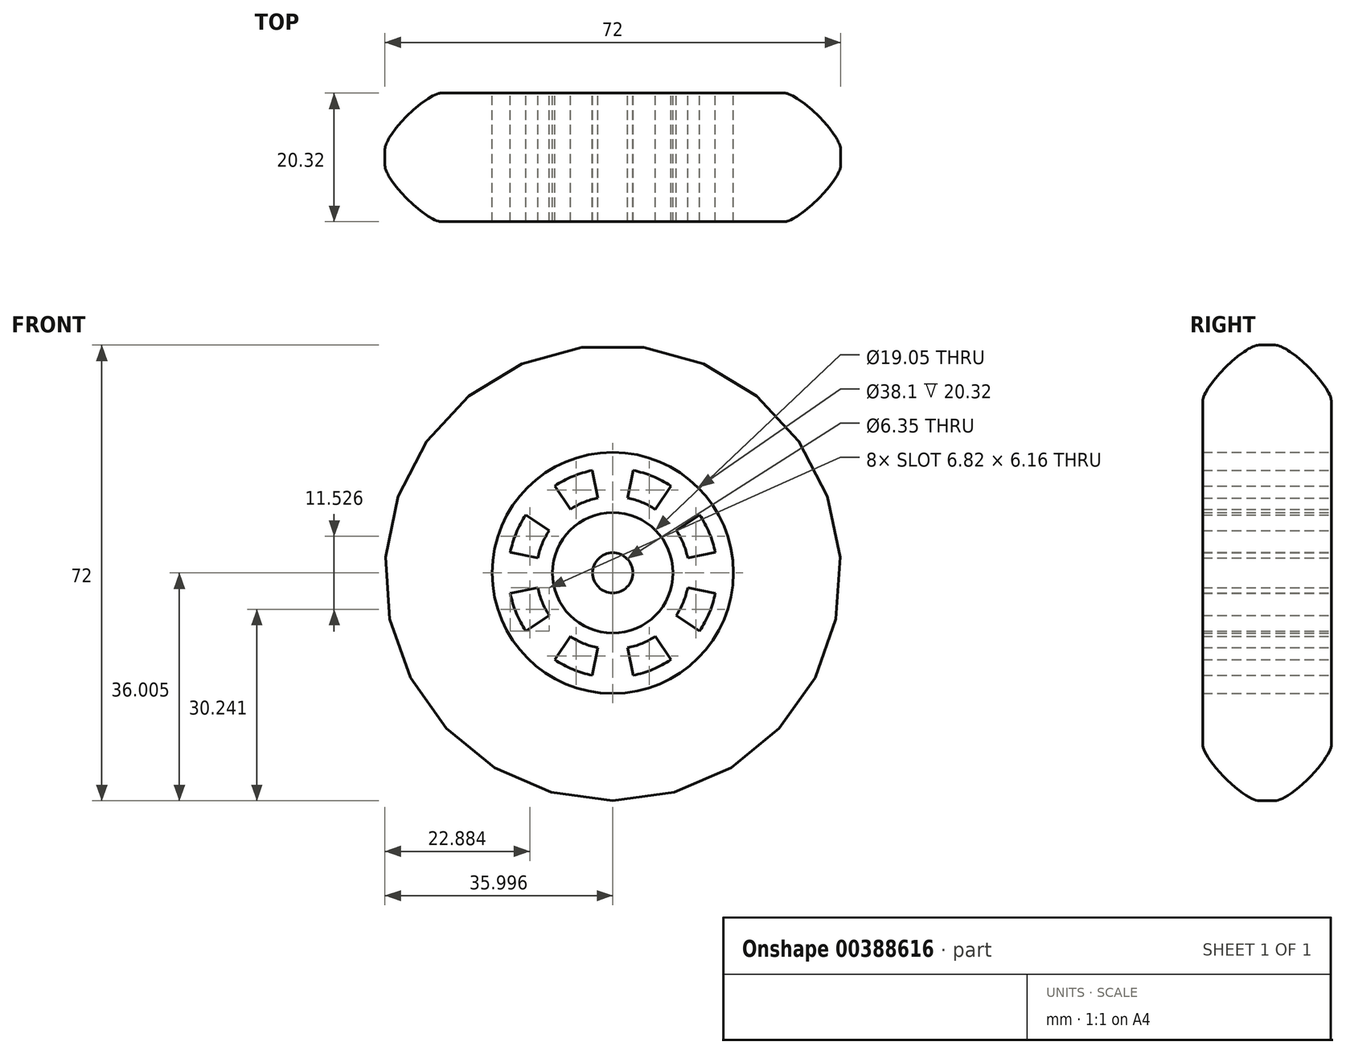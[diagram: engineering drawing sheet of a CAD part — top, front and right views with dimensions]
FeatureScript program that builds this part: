
annotation { "Feature Type Name" : "Feature", "Feature Type Description" : "" }
export const myFeature = defineFeature(function(context is Context, id is Id, definition is map)
    precondition{}
    {
        {
            var Q0;
            Q0=qCreatedBy(makeId("Front.planeOp"),FACE);
            var sketch = newSketch(context, id + "F0", { "sketchPlane" : qUnion([Q0])});
            skCircle(sketch, "E0", {"center": v(-20.8, 25.46) * mm, "radius": 36 * mm});
            skCircle(sketch, "E1", {"center": v(-20.8, 25.46) * mm, "radius": 19.05 * mm});
            skCircle(sketch, "E2", {"center": v(-20.8, 25.46) * mm, "radius": 9.53 * mm});
            skCircle(sketch, "E3", {"center": v(-20.8, 25.46) * mm, "radius": 3.18 * mm});
            skCircle(sketch, "E4", {"center": v(-20.8, 25.46) * mm, "radius": 16.51 * mm});
            skCircle(sketch, "E5", {"center": v(-20.8, 25.46) * mm, "radius": 12.07 * mm});
            skPoint(sketch, "E6.0.midPoint", {"position": v(-20.8, 41.97) * mm});
            skLineSegment(sketch, "E7", {"start": v(-30.15, 39.46) * mm, "end": v(-20.8, 25.46) * mm});
            skLineSegment(sketch, "E8", {"start": v(-24.08, 41.97) * mm, "end": v(-20.8, 25.46) * mm});
            skLineSegment(sketch, "E9", {"start": v(-17.5, 41.97) * mm, "end": v(-20.8, 25.46) * mm});
            skLineSegment(sketch, "E10", {"start": v(-11.44, 39.46) * mm, "end": v(-20.8, 25.46) * mm});
            skLineSegment(sketch, "E11", {"start": v(-6.8, 34.82) * mm, "end": v(-20.8, 25.46) * mm});
            skLineSegment(sketch, "E12", {"start": v(-4.28, 28.75) * mm, "end": v(-20.8, 25.46) * mm});
            skLineSegment(sketch, "E13", {"start": v(-4.28, 22.18) * mm, "end": v(-20.8, 25.46) * mm});
            skLineSegment(sketch, "E14", {"start": v(-6.8, 16.11) * mm, "end": v(-20.8, 25.46) * mm});
            skLineSegment(sketch, "E15", {"start": v(-11.44, 11.47) * mm, "end": v(-20.8, 25.46) * mm});
            skLineSegment(sketch, "E16", {"start": v(-17.5, 8.95) * mm, "end": v(-20.8, 25.46) * mm});
            skLineSegment(sketch, "E17", {"start": v(-24.08, 8.95) * mm, "end": v(-20.8, 25.46) * mm});
            skLineSegment(sketch, "E18", {"start": v(-30.15, 11.47) * mm, "end": v(-20.8, 25.46) * mm});
            skLineSegment(sketch, "E19", {"start": v(-34.8, 16.11) * mm, "end": v(-20.8, 25.46) * mm});
            skLineSegment(sketch, "E20", {"start": v(-37.3, 22.18) * mm, "end": v(-20.8, 25.46) * mm});
            skLineSegment(sketch, "E21", {"start": v(-37.3, 28.75) * mm, "end": v(-20.8, 25.46) * mm});
            skLineSegment(sketch, "E22", {"start": v(-34.8, 34.82) * mm, "end": v(-20.8, 25.46) * mm});
            skSolve(sketch);
        }
        {
            var Q0;
            {var subQ0=sQuery(id+"F0.wireOp",EDGE,"E8");var subQ1=sQuery(id+"F0.wireOp",EDGE,"E2");var subQ2=makeQuery(id+"F0.imprint","INTERSECT",VERTEX,{"derivedFrom":[subQ1,subQ0]});Q0=makeQuery(id+"F0.imprint","IMPRINT",FACE,{"disambiguationData":[TD([[makeQuery(id+"F0.imprint","IMPRINT",EDGE,{"disambiguationData":[TD([[subQ2,-1.0]])],"derivedFrom":subQ1}),1.0]])]});}
            var Q1;
            {var subQ0=sQuery(id+"F0.wireOp",EDGE,"E9");var subQ1=sQuery(id+"F0.wireOp",EDGE,"E2");var subQ2=makeQuery(id+"F0.imprint","INTERSECT",VERTEX,{"derivedFrom":[subQ1,subQ0]});Q1=makeQuery(id+"F0.imprint","IMPRINT",FACE,{"disambiguationData":[TD([[makeQuery(id+"F0.imprint","IMPRINT",EDGE,{"disambiguationData":[TD([[subQ2,-1.0]])],"derivedFrom":subQ1}),1.0]])]});}
            var Q2;
            {var subQ0=sQuery(id+"F0.wireOp",EDGE,"E10");var subQ1=sQuery(id+"F0.wireOp",EDGE,"E2");var subQ2=makeQuery(id+"F0.imprint","INTERSECT",VERTEX,{"derivedFrom":[subQ1,subQ0]});Q2=makeQuery(id+"F0.imprint","IMPRINT",FACE,{"disambiguationData":[TD([[makeQuery(id+"F0.imprint","IMPRINT",EDGE,{"disambiguationData":[TD([[subQ2,-1.0]])],"derivedFrom":subQ1}),1.0]])]});}
            var Q3;
            {var subQ0=sQuery(id+"F0.wireOp",EDGE,"E11");var subQ1=sQuery(id+"F0.wireOp",EDGE,"E2");var subQ2=makeQuery(id+"F0.imprint","INTERSECT",VERTEX,{"derivedFrom":[subQ1,subQ0]});Q3=makeQuery(id+"F0.imprint","IMPRINT",FACE,{"disambiguationData":[TD([[makeQuery(id+"F0.imprint","IMPRINT",EDGE,{"disambiguationData":[TD([[subQ2,-1.0]])],"derivedFrom":subQ1}),1.0]])]});}
            var Q4;
            {var subQ0=sQuery(id+"F0.wireOp",EDGE,"E11");var subQ1=sQuery(id+"F0.wireOp",EDGE,"E2");var subQ2=makeQuery(id+"F0.imprint","INTERSECT",VERTEX,{"derivedFrom":[subQ1,subQ0]});Q4=makeQuery(id+"F0.imprint","IMPRINT",FACE,{"disambiguationData":[TD([[makeQuery(id+"F0.imprint","IMPRINT",EDGE,{"disambiguationData":[TD([[subQ2,1.0]])],"derivedFrom":subQ1}),1.0]])]});}
            var Q5;
            {var subQ0=sQuery(id+"F0.wireOp",EDGE,"E7");var subQ1=sQuery(id+"F0.wireOp",EDGE,"E2");var subQ2=makeQuery(id+"F0.imprint","INTERSECT",VERTEX,{"derivedFrom":[subQ1,subQ0]});Q5=makeQuery(id+"F0.imprint","IMPRINT",FACE,{"disambiguationData":[TD([[makeQuery(id+"F0.imprint","IMPRINT",EDGE,{"disambiguationData":[TD([[subQ2,-1.0]])],"derivedFrom":subQ1}),1.0]])]});}
            var Q6;
            {var subQ0=sQuery(id+"F0.wireOp",EDGE,"E22");var subQ1=sQuery(id+"F0.wireOp",EDGE,"E2");var subQ2=makeQuery(id+"F0.imprint","INTERSECT",VERTEX,{"derivedFrom":[subQ1,subQ0]});Q6=makeQuery(id+"F0.imprint","IMPRINT",FACE,{"disambiguationData":[TD([[makeQuery(id+"F0.imprint","IMPRINT",EDGE,{"disambiguationData":[TD([[subQ2,-1.0]])],"derivedFrom":subQ1}),1.0]])]});}
            var Q7;
            {var subQ0=sQuery(id+"F0.wireOp",EDGE,"E21");var subQ1=sQuery(id+"F0.wireOp",EDGE,"E2");var subQ2=makeQuery(id+"F0.imprint","INTERSECT",VERTEX,{"derivedFrom":[subQ1,subQ0]});Q7=makeQuery(id+"F0.imprint","IMPRINT",FACE,{"disambiguationData":[TD([[makeQuery(id+"F0.imprint","IMPRINT",EDGE,{"disambiguationData":[TD([[subQ2,-1.0]])],"derivedFrom":subQ1}),1.0]])]});}
            var Q8;
            {var subQ0=sQuery(id+"F0.wireOp",EDGE,"E20");var subQ1=sQuery(id+"F0.wireOp",EDGE,"E2");var subQ2=makeQuery(id+"F0.imprint","INTERSECT",VERTEX,{"derivedFrom":[subQ1,subQ0]});Q8=makeQuery(id+"F0.imprint","IMPRINT",FACE,{"disambiguationData":[TD([[makeQuery(id+"F0.imprint","IMPRINT",EDGE,{"disambiguationData":[TD([[subQ2,-1.0]])],"derivedFrom":subQ1}),1.0]])]});}
            var Q9;
            {var subQ0=sQuery(id+"F0.wireOp",EDGE,"E19");var subQ1=sQuery(id+"F0.wireOp",EDGE,"E2");var subQ2=makeQuery(id+"F0.imprint","INTERSECT",VERTEX,{"derivedFrom":[subQ1,subQ0]});Q9=makeQuery(id+"F0.imprint","IMPRINT",FACE,{"disambiguationData":[TD([[makeQuery(id+"F0.imprint","IMPRINT",EDGE,{"disambiguationData":[TD([[subQ2,-1.0]])],"derivedFrom":subQ1}),1.0]])]});}
            var Q10;
            {var subQ0=sQuery(id+"F0.wireOp",EDGE,"E18");var subQ1=sQuery(id+"F0.wireOp",EDGE,"E2");var subQ2=makeQuery(id+"F0.imprint","INTERSECT",VERTEX,{"derivedFrom":[subQ1,subQ0]});Q10=makeQuery(id+"F0.imprint","IMPRINT",FACE,{"disambiguationData":[TD([[makeQuery(id+"F0.imprint","IMPRINT",EDGE,{"disambiguationData":[TD([[subQ2,-1.0]])],"derivedFrom":subQ1}),1.0]])]});}
            var Q11;
            {var subQ0=sQuery(id+"F0.wireOp",EDGE,"E17");var subQ1=sQuery(id+"F0.wireOp",EDGE,"E2");var subQ2=makeQuery(id+"F0.imprint","INTERSECT",VERTEX,{"derivedFrom":[subQ1,subQ0]});Q11=makeQuery(id+"F0.imprint","IMPRINT",FACE,{"disambiguationData":[TD([[makeQuery(id+"F0.imprint","IMPRINT",EDGE,{"disambiguationData":[TD([[subQ2,-1.0]])],"derivedFrom":subQ1}),1.0]])]});}
            var Q12;
            {var subQ0=sQuery(id+"F0.wireOp",EDGE,"E16");var subQ1=sQuery(id+"F0.wireOp",EDGE,"E2");var subQ2=makeQuery(id+"F0.imprint","INTERSECT",VERTEX,{"derivedFrom":[subQ1,subQ0]});Q12=makeQuery(id+"F0.imprint","IMPRINT",FACE,{"disambiguationData":[TD([[makeQuery(id+"F0.imprint","IMPRINT",EDGE,{"disambiguationData":[TD([[subQ2,-1.0]])],"derivedFrom":subQ1}),1.0]])]});}
            var Q13;
            {var subQ0=sQuery(id+"F0.wireOp",EDGE,"E15");var subQ1=sQuery(id+"F0.wireOp",EDGE,"E2");var subQ2=makeQuery(id+"F0.imprint","INTERSECT",VERTEX,{"derivedFrom":[subQ1,subQ0]});Q13=makeQuery(id+"F0.imprint","IMPRINT",FACE,{"disambiguationData":[TD([[makeQuery(id+"F0.imprint","IMPRINT",EDGE,{"disambiguationData":[TD([[subQ2,-1.0]])],"derivedFrom":subQ1}),1.0]])]});}
            var Q14;
            {var subQ0=sQuery(id+"F0.wireOp",EDGE,"E14");var subQ1=sQuery(id+"F0.wireOp",EDGE,"E2");var subQ2=makeQuery(id+"F0.imprint","INTERSECT",VERTEX,{"derivedFrom":[subQ1,subQ0]});Q14=makeQuery(id+"F0.imprint","IMPRINT",FACE,{"disambiguationData":[TD([[makeQuery(id+"F0.imprint","IMPRINT",EDGE,{"disambiguationData":[TD([[subQ2,-1.0]])],"derivedFrom":subQ1}),1.0]])]});}
            var Q15;
            {var subQ0=sQuery(id+"F0.wireOp",EDGE,"E12");var subQ1=sQuery(id+"F0.wireOp",EDGE,"E2");var subQ2=makeQuery(id+"F0.imprint","INTERSECT",VERTEX,{"derivedFrom":[subQ1,subQ0]});Q15=makeQuery(id+"F0.imprint","IMPRINT",FACE,{"disambiguationData":[TD([[makeQuery(id+"F0.imprint","IMPRINT",EDGE,{"disambiguationData":[TD([[subQ2,1.0]])],"derivedFrom":subQ1}),1.0]])]});}
            extrude(context, id + "F1", {"entities" : qUnion([Q0, Q1, Q2, Q3, Q4, Q5, Q6, Q7, Q8, Q9, Q10, Q11, Q12, Q13, Q14, Q15]), "depth" : 20.32 * mm});
        }
        {
            var Q0;
            {var subQ0=sQuery(id+"F0.wireOp",EDGE,"E8");var subQ1=sQuery(id+"F0.wireOp",EDGE,"E2");var subQ2=makeQuery(id+"F0.imprint","INTERSECT",VERTEX,{"derivedFrom":[subQ1,subQ0]});Q0=makeQuery(id+"F0.imprint","IMPRINT",FACE,{"disambiguationData":[TD([[makeQuery(id+"F0.imprint","IMPRINT",EDGE,{"disambiguationData":[TD([[subQ2,-1.0]])],"derivedFrom":subQ1}),-1.0]])]});}
            var Q1;
            {var subQ0=sQuery(id+"F0.wireOp",EDGE,"E7");var subQ1=sQuery(id+"F0.wireOp",EDGE,"E2");var subQ2=makeQuery(id+"F0.imprint","INTERSECT",VERTEX,{"derivedFrom":[subQ1,subQ0]});Q1=makeQuery(id+"F0.imprint","IMPRINT",FACE,{"disambiguationData":[TD([[makeQuery(id+"F0.imprint","IMPRINT",EDGE,{"disambiguationData":[TD([[subQ2,-1.0]])],"derivedFrom":subQ1}),-1.0]])]});}
            var Q2;
            {var subQ0=sQuery(id+"F0.wireOp",EDGE,"E7");var subQ1=sQuery(id+"F0.wireOp",EDGE,"E4");var subQ2=makeQuery(id+"F0.imprint","INTERSECT",VERTEX,{"derivedFrom":[subQ1,subQ0]});Q2=makeQuery(id+"F0.imprint","IMPRINT",FACE,{"disambiguationData":[TD([[makeQuery(id+"F0.imprint","IMPRINT",EDGE,{"disambiguationData":[TD([[subQ2,-1.0]])],"derivedFrom":subQ1}),1.0]])]});}
            var Q3;
            {var subQ0=sQuery(id+"F0.wireOp",EDGE,"E22");var subQ1=sQuery(id+"F0.wireOp",EDGE,"E2");var subQ2=makeQuery(id+"F0.imprint","INTERSECT",VERTEX,{"derivedFrom":[subQ1,subQ0]});Q3=makeQuery(id+"F0.imprint","IMPRINT",FACE,{"disambiguationData":[TD([[makeQuery(id+"F0.imprint","IMPRINT",EDGE,{"disambiguationData":[TD([[subQ2,-1.0]])],"derivedFrom":subQ1}),-1.0]])]});}
            var Q4;
            {var subQ0=sQuery(id+"F0.wireOp",EDGE,"E21");var subQ1=sQuery(id+"F0.wireOp",EDGE,"E4");var subQ2=makeQuery(id+"F0.imprint","INTERSECT",VERTEX,{"derivedFrom":[subQ1,subQ0]});Q4=makeQuery(id+"F0.imprint","IMPRINT",FACE,{"disambiguationData":[TD([[makeQuery(id+"F0.imprint","IMPRINT",EDGE,{"disambiguationData":[TD([[subQ2,-1.0]])],"derivedFrom":subQ1}),1.0]])]});}
            var Q5;
            {var subQ0=sQuery(id+"F0.wireOp",EDGE,"E21");var subQ1=sQuery(id+"F0.wireOp",EDGE,"E2");var subQ2=makeQuery(id+"F0.imprint","INTERSECT",VERTEX,{"derivedFrom":[subQ1,subQ0]});Q5=makeQuery(id+"F0.imprint","IMPRINT",FACE,{"disambiguationData":[TD([[makeQuery(id+"F0.imprint","IMPRINT",EDGE,{"disambiguationData":[TD([[subQ2,-1.0]])],"derivedFrom":subQ1}),-1.0]])]});}
            var Q6;
            {var subQ0=sQuery(id+"F0.wireOp",EDGE,"E20");var subQ1=sQuery(id+"F0.wireOp",EDGE,"E2");var subQ2=makeQuery(id+"F0.imprint","INTERSECT",VERTEX,{"derivedFrom":[subQ1,subQ0]});Q6=makeQuery(id+"F0.imprint","IMPRINT",FACE,{"disambiguationData":[TD([[makeQuery(id+"F0.imprint","IMPRINT",EDGE,{"disambiguationData":[TD([[subQ2,-1.0]])],"derivedFrom":subQ1}),-1.0]])]});}
            var Q7;
            {var subQ0=sQuery(id+"F0.wireOp",EDGE,"E19");var subQ1=sQuery(id+"F0.wireOp",EDGE,"E2");var subQ2=makeQuery(id+"F0.imprint","INTERSECT",VERTEX,{"derivedFrom":[subQ1,subQ0]});Q7=makeQuery(id+"F0.imprint","IMPRINT",FACE,{"disambiguationData":[TD([[makeQuery(id+"F0.imprint","IMPRINT",EDGE,{"disambiguationData":[TD([[subQ2,-1.0]])],"derivedFrom":subQ1}),-1.0]])]});}
            var Q8;
            {var subQ0=sQuery(id+"F0.wireOp",EDGE,"E19");var subQ1=sQuery(id+"F0.wireOp",EDGE,"E4");var subQ2=makeQuery(id+"F0.imprint","INTERSECT",VERTEX,{"derivedFrom":[subQ1,subQ0]});Q8=makeQuery(id+"F0.imprint","IMPRINT",FACE,{"disambiguationData":[TD([[makeQuery(id+"F0.imprint","IMPRINT",EDGE,{"disambiguationData":[TD([[subQ2,-1.0]])],"derivedFrom":subQ1}),1.0]])]});}
            var Q9;
            {var subQ0=sQuery(id+"F0.wireOp",EDGE,"E18");var subQ1=sQuery(id+"F0.wireOp",EDGE,"E2");var subQ2=makeQuery(id+"F0.imprint","INTERSECT",VERTEX,{"derivedFrom":[subQ1,subQ0]});Q9=makeQuery(id+"F0.imprint","IMPRINT",FACE,{"disambiguationData":[TD([[makeQuery(id+"F0.imprint","IMPRINT",EDGE,{"disambiguationData":[TD([[subQ2,-1.0]])],"derivedFrom":subQ1}),-1.0]])]});}
            var Q10;
            {var subQ0=sQuery(id+"F0.wireOp",EDGE,"E17");var subQ1=sQuery(id+"F0.wireOp",EDGE,"E2");var subQ2=makeQuery(id+"F0.imprint","INTERSECT",VERTEX,{"derivedFrom":[subQ1,subQ0]});Q10=makeQuery(id+"F0.imprint","IMPRINT",FACE,{"disambiguationData":[TD([[makeQuery(id+"F0.imprint","IMPRINT",EDGE,{"disambiguationData":[TD([[subQ2,-1.0]])],"derivedFrom":subQ1}),-1.0]])]});}
            var Q11;
            {var subQ0=sQuery(id+"F0.wireOp",EDGE,"E17");var subQ1=sQuery(id+"F0.wireOp",EDGE,"E4");var subQ2=makeQuery(id+"F0.imprint","INTERSECT",VERTEX,{"derivedFrom":[subQ1,subQ0]});Q11=makeQuery(id+"F0.imprint","IMPRINT",FACE,{"disambiguationData":[TD([[makeQuery(id+"F0.imprint","IMPRINT",EDGE,{"disambiguationData":[TD([[subQ2,-1.0]])],"derivedFrom":subQ1}),1.0]])]});}
            var Q12;
            {var subQ0=sQuery(id+"F0.wireOp",EDGE,"E16");var subQ1=sQuery(id+"F0.wireOp",EDGE,"E2");var subQ2=makeQuery(id+"F0.imprint","INTERSECT",VERTEX,{"derivedFrom":[subQ1,subQ0]});Q12=makeQuery(id+"F0.imprint","IMPRINT",FACE,{"disambiguationData":[TD([[makeQuery(id+"F0.imprint","IMPRINT",EDGE,{"disambiguationData":[TD([[subQ2,-1.0]])],"derivedFrom":subQ1}),-1.0]])]});}
            var Q13;
            {var subQ0=sQuery(id+"F0.wireOp",EDGE,"E15");var subQ1=sQuery(id+"F0.wireOp",EDGE,"E2");var subQ2=makeQuery(id+"F0.imprint","INTERSECT",VERTEX,{"derivedFrom":[subQ1,subQ0]});Q13=makeQuery(id+"F0.imprint","IMPRINT",FACE,{"disambiguationData":[TD([[makeQuery(id+"F0.imprint","IMPRINT",EDGE,{"disambiguationData":[TD([[subQ2,-1.0]])],"derivedFrom":subQ1}),-1.0]])]});}
            var Q14;
            {var subQ0=sQuery(id+"F0.wireOp",EDGE,"E14");var subQ1=sQuery(id+"F0.wireOp",EDGE,"E2");var subQ2=makeQuery(id+"F0.imprint","INTERSECT",VERTEX,{"derivedFrom":[subQ1,subQ0]});Q14=makeQuery(id+"F0.imprint","IMPRINT",FACE,{"disambiguationData":[TD([[makeQuery(id+"F0.imprint","IMPRINT",EDGE,{"disambiguationData":[TD([[subQ2,-1.0]])],"derivedFrom":subQ1}),-1.0]])]});}
            var Q15;
            {var subQ0=sQuery(id+"F0.wireOp",EDGE,"E12");var subQ1=sQuery(id+"F0.wireOp",EDGE,"E2");var subQ2=makeQuery(id+"F0.imprint","INTERSECT",VERTEX,{"derivedFrom":[subQ1,subQ0]});Q15=makeQuery(id+"F0.imprint","IMPRINT",FACE,{"disambiguationData":[TD([[makeQuery(id+"F0.imprint","IMPRINT",EDGE,{"disambiguationData":[TD([[subQ2,1.0]])],"derivedFrom":subQ1}),-1.0]])]});}
            var Q16;
            {var subQ0=sQuery(id+"F0.wireOp",EDGE,"E11");var subQ1=sQuery(id+"F0.wireOp",EDGE,"E2");var subQ2=makeQuery(id+"F0.imprint","INTERSECT",VERTEX,{"derivedFrom":[subQ1,subQ0]});Q16=makeQuery(id+"F0.imprint","IMPRINT",FACE,{"disambiguationData":[TD([[makeQuery(id+"F0.imprint","IMPRINT",EDGE,{"disambiguationData":[TD([[subQ2,1.0]])],"derivedFrom":subQ1}),-1.0]])]});}
            var Q17;
            {var subQ0=sQuery(id+"F0.wireOp",EDGE,"E11");var subQ1=sQuery(id+"F0.wireOp",EDGE,"E2");var subQ2=makeQuery(id+"F0.imprint","INTERSECT",VERTEX,{"derivedFrom":[subQ1,subQ0]});Q17=makeQuery(id+"F0.imprint","IMPRINT",FACE,{"disambiguationData":[TD([[makeQuery(id+"F0.imprint","IMPRINT",EDGE,{"disambiguationData":[TD([[subQ2,-1.0]])],"derivedFrom":subQ1}),-1.0]])]});}
            var Q18;
            {var subQ0=sQuery(id+"F0.wireOp",EDGE,"E10");var subQ1=sQuery(id+"F0.wireOp",EDGE,"E2");var subQ2=makeQuery(id+"F0.imprint","INTERSECT",VERTEX,{"derivedFrom":[subQ1,subQ0]});Q18=makeQuery(id+"F0.imprint","IMPRINT",FACE,{"disambiguationData":[TD([[makeQuery(id+"F0.imprint","IMPRINT",EDGE,{"disambiguationData":[TD([[subQ2,-1.0]])],"derivedFrom":subQ1}),-1.0]])]});}
            var Q19;
            {var subQ0=sQuery(id+"F0.wireOp",EDGE,"E9");var subQ1=sQuery(id+"F0.wireOp",EDGE,"E2");var subQ2=makeQuery(id+"F0.imprint","INTERSECT",VERTEX,{"derivedFrom":[subQ1,subQ0]});Q19=makeQuery(id+"F0.imprint","IMPRINT",FACE,{"disambiguationData":[TD([[makeQuery(id+"F0.imprint","IMPRINT",EDGE,{"disambiguationData":[TD([[subQ2,-1.0]])],"derivedFrom":subQ1}),-1.0]])]});}
            var Q20;
            {var subQ0=sQuery(id+"F0.wireOp",EDGE,"E9");var subQ1=sQuery(id+"F0.wireOp",EDGE,"E4");var subQ2=makeQuery(id+"F0.imprint","INTERSECT",VERTEX,{"derivedFrom":[subQ1,subQ0]});Q20=makeQuery(id+"F0.imprint","IMPRINT",FACE,{"disambiguationData":[TD([[makeQuery(id+"F0.imprint","IMPRINT",EDGE,{"disambiguationData":[TD([[subQ2,-1.0]])],"derivedFrom":subQ1}),1.0]])]});}
            var Q21;
            {var subQ0=sQuery(id+"F0.wireOp",EDGE,"E11");var subQ1=sQuery(id+"F0.wireOp",EDGE,"E4");var subQ2=makeQuery(id+"F0.imprint","INTERSECT",VERTEX,{"derivedFrom":[subQ1,subQ0]});Q21=makeQuery(id+"F0.imprint","IMPRINT",FACE,{"disambiguationData":[TD([[makeQuery(id+"F0.imprint","IMPRINT",EDGE,{"disambiguationData":[TD([[subQ2,-1.0]])],"derivedFrom":subQ1}),1.0]])]});}
            var Q22;
            {var subQ0=sQuery(id+"F0.wireOp",EDGE,"E12");var subQ1=sQuery(id+"F0.wireOp",EDGE,"E4");var subQ2=makeQuery(id+"F0.imprint","INTERSECT",VERTEX,{"derivedFrom":[subQ1,subQ0]});Q22=makeQuery(id+"F0.imprint","IMPRINT",FACE,{"disambiguationData":[TD([[makeQuery(id+"F0.imprint","IMPRINT",EDGE,{"disambiguationData":[TD([[subQ2,1.0]])],"derivedFrom":subQ1}),1.0]])]});}
            var Q23;
            {var subQ0=sQuery(id+"F0.wireOp",EDGE,"E15");var subQ1=sQuery(id+"F0.wireOp",EDGE,"E4");var subQ2=makeQuery(id+"F0.imprint","INTERSECT",VERTEX,{"derivedFrom":[subQ1,subQ0]});Q23=makeQuery(id+"F0.imprint","IMPRINT",FACE,{"disambiguationData":[TD([[makeQuery(id+"F0.imprint","IMPRINT",EDGE,{"disambiguationData":[TD([[subQ2,-1.0]])],"derivedFrom":subQ1}),1.0]])]});}
            var Q24;
            Q24=makeQuery(id+"F0.imprint","IMPRINT",FACE,{"disambiguationData":[TD([[makeQuery(id+"F0.imprint","IMPRINT",EDGE,{"derivedFrom":sQuery(id+"F0.wireOp",EDGE,"E1")}),1.0]])]});
            extrude(context, id + "F2", {"entities" : qUnion([Q0, Q1, Q2, Q3, Q4, Q5, Q6, Q7, Q8, Q9, Q10, Q11, Q12, Q13, Q14, Q15, Q16, Q17, Q18, Q19, Q20, Q21, Q22, Q23, Q24]), "depth" : 20.32 * mm});
        }
        {
            var Q0;
            Q0=makeQuery(id+"F0.imprint","IMPRINT",FACE,{"disambiguationData":[TD([[makeQuery(id+"F0.imprint","IMPRINT",EDGE,{"derivedFrom":sQuery(id+"F0.wireOp",EDGE,"E0")}),1.0]])]});
            extrude(context, id + "F3", {"entities" : qUnion([Q0]), "depth" : 20.32 * mm});
        }
        {
            var Q0;
            Q0=makeQuery(id+"F3.opExtrude","CAP_EDGE",EDGE,{"disambiguationData":[OSD([sQuery(id+"F0.wireOp",EDGE,"E0")])],"isStart":false});
            var Q1;
            Q1=makeQuery(id+"F3.opExtrude","CAP_EDGE",EDGE,{"disambiguationData":[OSD([sQuery(id+"F0.wireOp",EDGE,"E0")])],"isStart":true});
            fillet(context, id + "F4", {"entities" : qUnion([Q0, Q1]), "radius" : 8.9 * mm, "tangentPropagation" : true, "rho" : .2, "crossSection" : FilletCrossSection.CONIC, "allowEdgeOverflow" : false});
        }
    });
